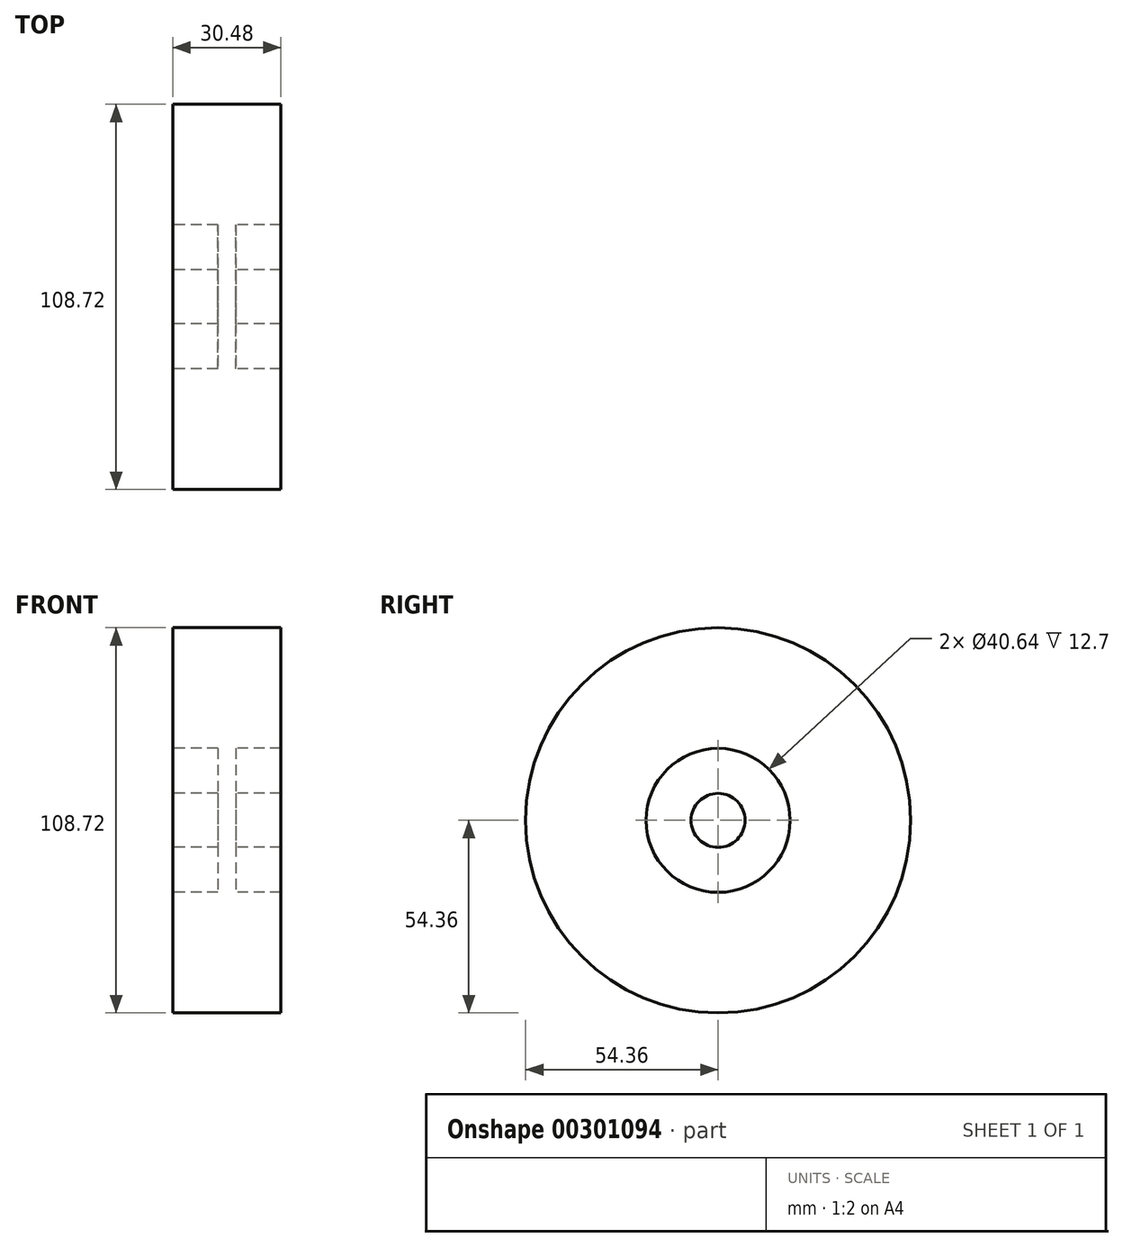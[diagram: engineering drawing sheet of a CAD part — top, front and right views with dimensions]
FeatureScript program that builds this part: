
annotation { "Feature Type Name" : "Feature", "Feature Type Description" : "" }
export const myFeature = defineFeature(function(context is Context, id is Id, definition is map)
    precondition{}
    {
        {
            var Q0;
            Q0=qCreatedBy(makeId("Front.planeOp"),FACE);
            var sketch = newSketch(context, id + "F0", { "sketchPlane" : qUnion([Q0])});
            skLineSegment(sketch, "E0", {"start": v(0, 0) * mm, "end": v(15.24, 0) * mm});
            skLineSegment(sketch, "E1", {"start": v(15.24, 0) * mm, "end": v(15.24, 7.62) * mm});
            skLineSegment(sketch, "E2", {"start": v(15.24, 7.62) * mm, "end": v(2.54, 7.62) * mm});
            skLineSegment(sketch, "E3", {"start": v(2.54, 7.62) * mm, "end": v(2.54, 20.32) * mm});
            skLineSegment(sketch, "E4", {"start": v(2.54, 20.32) * mm, "end": v(15.24, 20.32) * mm});
            skLineSegment(sketch, "E5", {"start": v(15.24, 20.32) * mm, "end": v(15.24, 54.36) * mm});
            skLineSegment(sketch, "E6", {"start": v(15.24, 54.36) * mm, "end": v(0, 54.36) * mm});
            skLineSegment(sketch, "E7.MirrorCS", {"start": v(0, 0) * mm, "end": v(-15.24, 0) * mm});
            skLineSegment(sketch, "E8.MirrorCS", {"start": v(-2.54, 20.32) * mm, "end": v(-15.24, 20.32) * mm});
            skLineSegment(sketch, "E9.MirrorCS", {"start": v(-2.54, 7.62) * mm, "end": v(-2.54, 20.32) * mm});
            skLineSegment(sketch, "E10.MirrorCS", {"start": v(-15.24, 20.32) * mm, "end": v(-15.24, 54.36) * mm});
            skLineSegment(sketch, "E11.MirrorCS", {"start": v(-15.24, 0) * mm, "end": v(-15.24, 7.62) * mm});
            skLineSegment(sketch, "E12.MirrorCS", {"start": v(-15.24, 7.62) * mm, "end": v(-2.54, 7.62) * mm});
            skLineSegment(sketch, "E13.MirrorCS", {"start": v(-15.24, 54.36) * mm, "end": v(0, 54.36) * mm});
            skSolve(sketch);
        }
        {
            var Q0;
            Q0=makeQuery(id+"F0.imprint","IMPRINT",FACE,{"disambiguationData":[TD([[makeQuery(id+"F0.imprint","IMPRINT",EDGE,{"derivedFrom":sQuery(id+"F0.wireOp",EDGE,"E0")}),1.0]])]});
            var Q1;
            Q1=sQuery(id+"F0.wireOp",EDGE,"E0");
            revolve(context, id + "F1", {"entities" : qUnion([Q0]), "axis" : qUnion([Q1]), "revolveType" : RevolveType.FULL});
        }
    });
